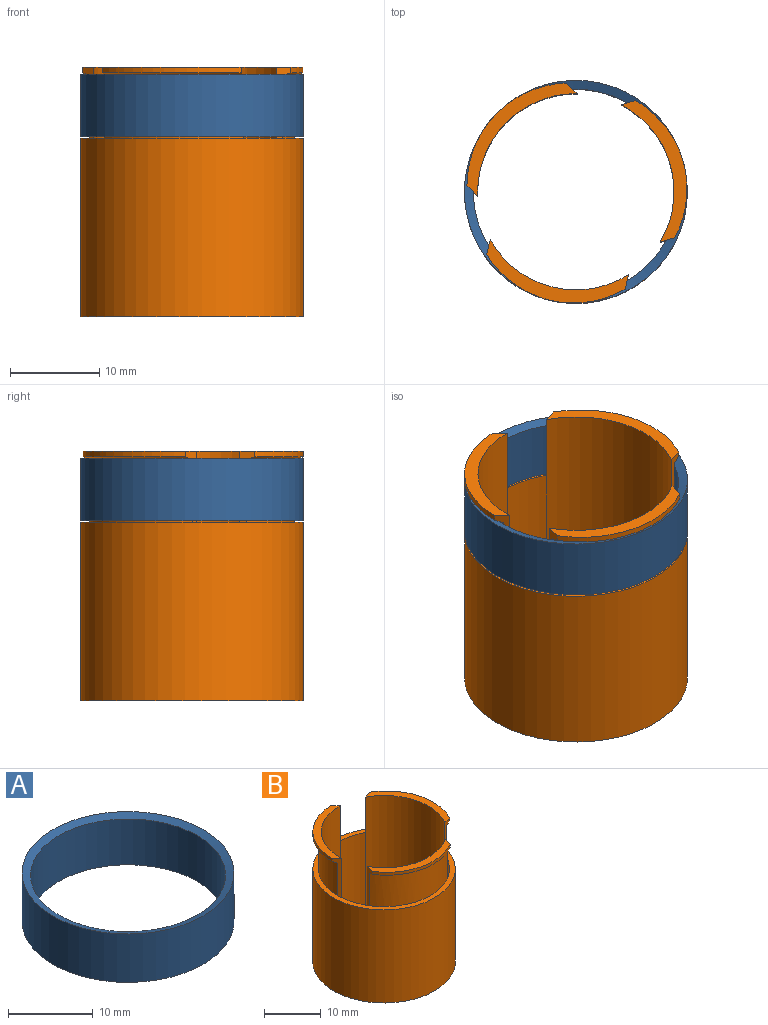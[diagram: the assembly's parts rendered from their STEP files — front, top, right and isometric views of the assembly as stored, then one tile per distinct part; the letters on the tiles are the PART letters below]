
ASSEMBLY  parts=2 mates=1
PART A: 4 faces, bbox 25x25x7 mm
  f0: cylinder r=12.5mm len=25mm, axis (0,0,-1), area 547.9mm2, adj f1,f3
  f1: plane 25x25mm, normal (0,0,-1), area 75.4mm2, adj f0,f2
  f2: cylinder r=11.5mm len=23mm, axis (0,0,-1), area 477.8mm2, adj f1,f3
  f3: cone r=11.5mm half-angle=70deg, axis (0,0,1), area 80.2mm2, adj f0,f2
PART B: 27 faces, bbox 25.3x25.3x28 mm
  f0: cylinder r=11.5mm len=20mm, axis (0,0,-1), area 127.8mm2, adj f3,f4,f14,f19
  f1: cylinder r=11.5mm len=20mm, axis (0,0,-1), area 127.8mm2, adj f3,f4,f8,f13
  f2: cylinder r=12.5mm len=25mm, axis (0,0,-1), area 1570.8mm2, adj f3,f4
  f3: plane 25x25mm, normal (0,0,1), area 75.4mm2, adj f0,f1,f2,f5,f6,f12,f18
  f4: plane 25x25mm, normal (0,0,-1), area 102.1mm2, adj f0,f1,f2,f5,f7,f8,f13,f14
  f5: cylinder r=11.5mm len=20mm, axis (0,0,-1), area 127.8mm2, adj f3,f4,f7,f20
  f6: cylinder r=11.5mm len=11.49mm, axis (0,0,-1), area 123.9mm2, adj f3,f7,f8,f10
  f7: plane 28x1.23mm, normal (0.7,0.72,0), area 20.7mm2, adj f4,f5,f6,f9,f10,f11,f26
  f8: plane 28x1.23mm, normal (-0.7,-0.72,0), area 20.7mm2, adj f1,f4,f6,f9,f10,f11,f26
  f9: plane 12.68x12.36mm, normal (0,0,1), area 24.8mm2, adj f7,f8,f11,f26
  f10: bspline ~12.19x11.85mm, area 17.3mm2, adj f6,f7,f8,f11
  f11: bspline ~11.49x11.13mm, area 11.2mm2, adj f7,f8,f9,f10
  f12: cylinder r=11.5mm len=15.52mm, axis (0,0,-1), area 123.9mm2, adj f3,f13,f14,f17
  f13: plane 28x1.66mm, normal (-0.97,0.24,0), area 20.7mm2, adj f1,f4,f12,f15,f16,f17,f25
  f14: plane 28x1.66mm, normal (0.97,-0.24,0), area 20.7mm2, adj f0,f4,f12,f15,f16,f17,f25
  f15: plane 15.94x7.23mm, normal (0,0,1), area 24.8mm2, adj f13,f14,f16,f25
  f16: bspline ~15.52x5.81mm, area 11.2mm2, adj f13,f14,f15,f17
  f17: bspline ~15.76x6.4mm, area 17.3mm2, adj f12,f13,f14,f16
  f18: cylinder r=11.5mm len=15.39mm, axis (0,0,-1), area 123.9mm2, adj f3,f19,f20,f23
  f19: plane 28x1.65mm, normal (0.27,-0.96,0), area 20.7mm2, adj f0,f4,f18,f21,f22,f23,f24
  f20: plane 28x1.65mm, normal (-0.27,0.96,0), area 20.7mm2, adj f4,f5,f18,f21,f22,f23,f24
  f21: plane 15.86x7.53mm, normal (0,0,1), area 24.8mm2, adj f19,f20,f22,f24
  f22: bspline ~15.39x6.12mm, area 11.2mm2, adj f19,f20,f21,f23
  f23: bspline ~15.66x7.08mm, area 17.3mm2, adj f18,f19,f20,f22
  f24: cylinder r=11mm len=28mm, axis (0,0,1), area 501.6mm2, adj f4,f19,f20,f21
  f25: cylinder r=11mm len=28mm, axis (0,0,1), area 501.6mm2, adj f4,f13,f14,f15
  f26: cylinder r=11mm len=28mm, axis (0,0,1), area 501.6mm2, adj f4,f7,f8,f9
PLACE A t=(0,0,20.19)mm
PLACE B at identity
MATE fastened B.f12 <-> A.f0  axis (0,0,-1) through (0,0,23.5)mm
